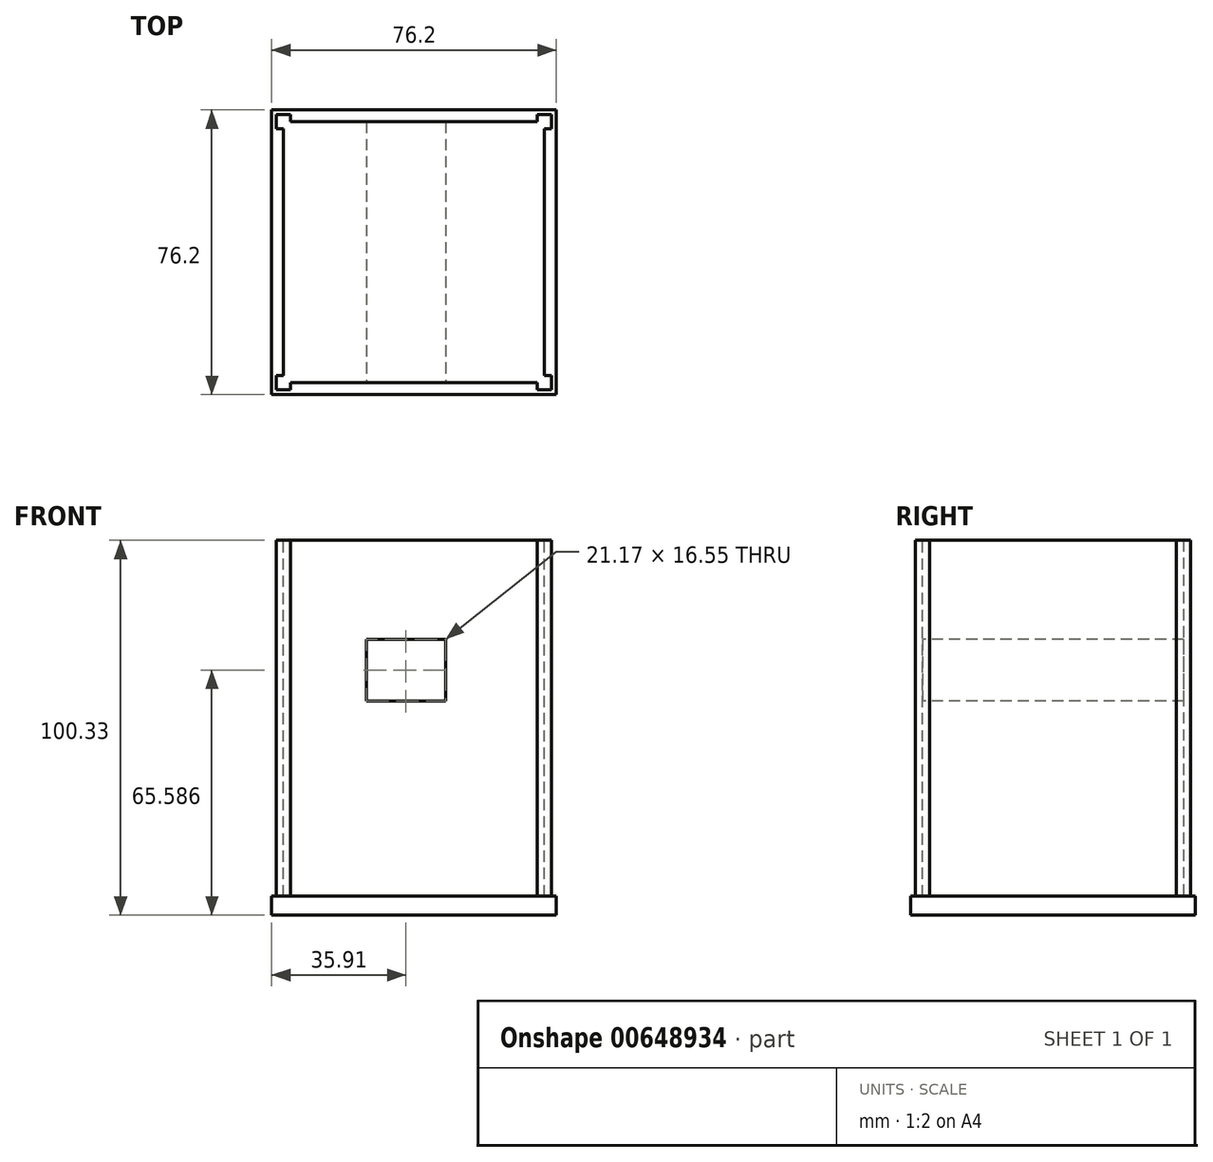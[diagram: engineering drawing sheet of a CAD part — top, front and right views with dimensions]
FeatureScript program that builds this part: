
annotation { "Feature Type Name" : "Feature", "Feature Type Description" : "" }
export const myFeature = defineFeature(function(context is Context, id is Id, definition is map)
    precondition{}
    {
        {
            var Q0;
            Q0=qCreatedBy(makeId("Top.planeOp"),FACE);
            var sketch = newSketch(context, id + "F0", { "sketchPlane" : qUnion([Q0])});
            skLineSegment(sketch, "E0.bottom", {"start": v(38.1, -38.1) * mm, "end": v(-38.1, -38.1) * mm});
            skLineSegment(sketch, "E0.top", {"start": v(38.1, 38.1) * mm, "end": v(-38.1, 38.1) * mm});
            skLineSegment(sketch, "E0.left", {"start": v(38.1, -38.1) * mm, "end": v(38.1, 38.1) * mm});
            skLineSegment(sketch, "E0.right", {"start": v(-38.1, -38.1) * mm, "end": v(-38.1, 38.1) * mm});
            skPoint(sketch, "E0.middle", {"position": v(0, 0) * mm});
            skSolve(sketch);
        }
        {
            var Q0;
            Q0=makeQuery(id+"F0.imprint","IMPRINT",FACE,{"disambiguationData":[TD([[makeQuery(id+"F0.imprint","IMPRINT",EDGE,{"derivedFrom":sQuery(id+"F0.wireOp",EDGE,"E0.bottom")}),-1.0]])]});
            extrude(context, id + "F1", {"entities" : qUnion([Q0]), "depth" : 5.08 * mm, "offsetDistance" : 25.4 * mm});
        }
        {
            var Q0;
            Q0=makeQuery(id+"F1.opExtrude","CAP_FACE",FACE,{"disambiguationData":[OSD([sQuery(id+"F0.wireOp",EDGE,"E0.bottom"),sQuery(id+"F0.wireOp",EDGE,"E0.top"),sQuery(id+"F0.wireOp",EDGE,"E0.left"),sQuery(id+"F0.wireOp",EDGE,"E0.right")])],"isStart":false});
            var sketch = newSketch(context, id + "F2", { "sketchPlane" : qUnion([Q0])});
            skLineSegment(sketch, "E1.bottom", {"start": v(34.93, -34.93) * mm, "end": v(-34.93, -34.93) * mm});
            skLineSegment(sketch, "E1.top", {"start": v(34.93, 34.93) * mm, "end": v(-34.92, 34.92) * mm});
            skLineSegment(sketch, "E1.left", {"start": v(34.93, -34.92) * mm, "end": v(34.93, 34.93) * mm});
            skLineSegment(sketch, "E1.right", {"start": v(-34.93, -34.93) * mm, "end": v(-34.93, 34.92) * mm});
            skPoint(sketch, "E1.middle", {"position": v(0, 0) * mm});
            skSolve(sketch);
        }
        {
            var Q0;
            Q0=makeQuery(id+"F2.imprint","IMPRINT",FACE,{"disambiguationData":[TD([[makeQuery(id+"F2.imprint","IMPRINT",EDGE,{"derivedFrom":sQuery(id+"F2.wireOp",EDGE,"E1.bottom")}),-1.0]])]});
            extrude(context, id + "F3", {"entities" : qUnion([Q0]), "operationType" : NewBodyOperationType.ADD, "depth" : 95.25 * mm, "offsetDistance" : 25.4 * mm});
        }
        {
            var Q0;
            Q0=qCreatedBy(makeId("Top.planeOp"),FACE);
            var sketch = newSketch(context, id + "F4", { "sketchPlane" : qUnion([Q0])});
            skPoint(sketch, "E2.0", {"position": v(34.93, 34.93) * mm});
            skPoint(sketch, "E3.0", {"position": v(-34.93, 34.92) * mm});
            skPoint(sketch, "E4.0", {"position": v(-34.93, -34.93) * mm});
            skPoint(sketch, "E5.0", {"position": v(34.93, -34.93) * mm});
            skLineSegment(sketch, "E6.bottom", {"start": v(36.83, -36.83) * mm, "end": v(33.02, -36.83) * mm});
            skLineSegment(sketch, "E6.top", {"start": v(36.83, -33.02) * mm, "end": v(33.02, -33.02) * mm});
            skLineSegment(sketch, "E6.left", {"start": v(36.83, -36.83) * mm, "end": v(36.83, -33.02) * mm});
            skLineSegment(sketch, "E6.right", {"start": v(33.02, -36.83) * mm, "end": v(33.02, -33.02) * mm});
            skLineSegment(sketch, "E7.bottom", {"start": v(-33.02, -33.02) * mm, "end": v(-36.83, -33.02) * mm});
            skLineSegment(sketch, "E7.top", {"start": v(-33.02, -36.83) * mm, "end": v(-36.83, -36.83) * mm});
            skLineSegment(sketch, "E7.left", {"start": v(-33.02, -33.02) * mm, "end": v(-33.02, -36.83) * mm});
            skLineSegment(sketch, "E7.right", {"start": v(-36.83, -33.02) * mm, "end": v(-36.83, -36.83) * mm});
            skLineSegment(sketch, "E8.bottom", {"start": v(-33.02, 33.02) * mm, "end": v(-36.83, 33.02) * mm});
            skLineSegment(sketch, "E8.top", {"start": v(-33.02, 36.83) * mm, "end": v(-36.83, 36.83) * mm});
            skLineSegment(sketch, "E8.left", {"start": v(-33.02, 33.02) * mm, "end": v(-33.02, 36.83) * mm});
            skLineSegment(sketch, "E8.right", {"start": v(-36.83, 33.02) * mm, "end": v(-36.83, 36.83) * mm});
            skLineSegment(sketch, "E9.bottom", {"start": v(36.83, 33.02) * mm, "end": v(33.02, 33.02) * mm});
            skLineSegment(sketch, "E9.top", {"start": v(36.83, 36.83) * mm, "end": v(33.02, 36.83) * mm});
            skLineSegment(sketch, "E9.left", {"start": v(36.83, 33.02) * mm, "end": v(36.83, 36.83) * mm});
            skLineSegment(sketch, "E9.right", {"start": v(33.02, 33.02) * mm, "end": v(33.02, 36.83) * mm});
            skSolve(sketch);
        }
        {
            var Q0;
            Q0 = qSketchRegion(id + "F4", true);
            extrude(context, id + "F5", {"entities" : qUnion([Q0]), "operationType" : NewBodyOperationType.ADD, "depth" : 100.33 * mm, "offsetDistance" : 25.4 * mm});
        }
        {
            var Q0;
            Q0=makeQuery(id+"F3.opExtrude","SWEPT_FACE",FACE,{"disambiguationData":[OSD([sQuery(id+"F2.wireOp",EDGE,"E1.bottom")])]});
            var sketch = newSketch(context, id + "F6", { "sketchPlane" : qUnion([Q0])});
            skLineSegment(sketch, "E10.bottom", {"start": v(-12.78, 73.86) * mm, "end": v(8.4, 73.86) * mm});
            skLineSegment(sketch, "E10.top", {"start": v(-12.78, 57.31) * mm, "end": v(8.4, 57.31) * mm});
            skLineSegment(sketch, "E10.left", {"start": v(-12.78, 73.86) * mm, "end": v(-12.78, 57.31) * mm});
            skLineSegment(sketch, "E10.right", {"start": v(8.4, 73.86) * mm, "end": v(8.4, 57.31) * mm});
            skSolve(sketch);
        }
        {
            var Q0;
            Q0 = qSketchRegion(id + "F6", true);
            extrude(context, id + "F7", {"entities" : qUnion([Q0]), "operationType" : NewBodyOperationType.REMOVE, "endBound" : BoundingType.THROUGH_ALL, "oppositeDirection" : true, "depth" : 25.4 * mm, "offsetDistance" : 25.4 * mm});
        }
    });
